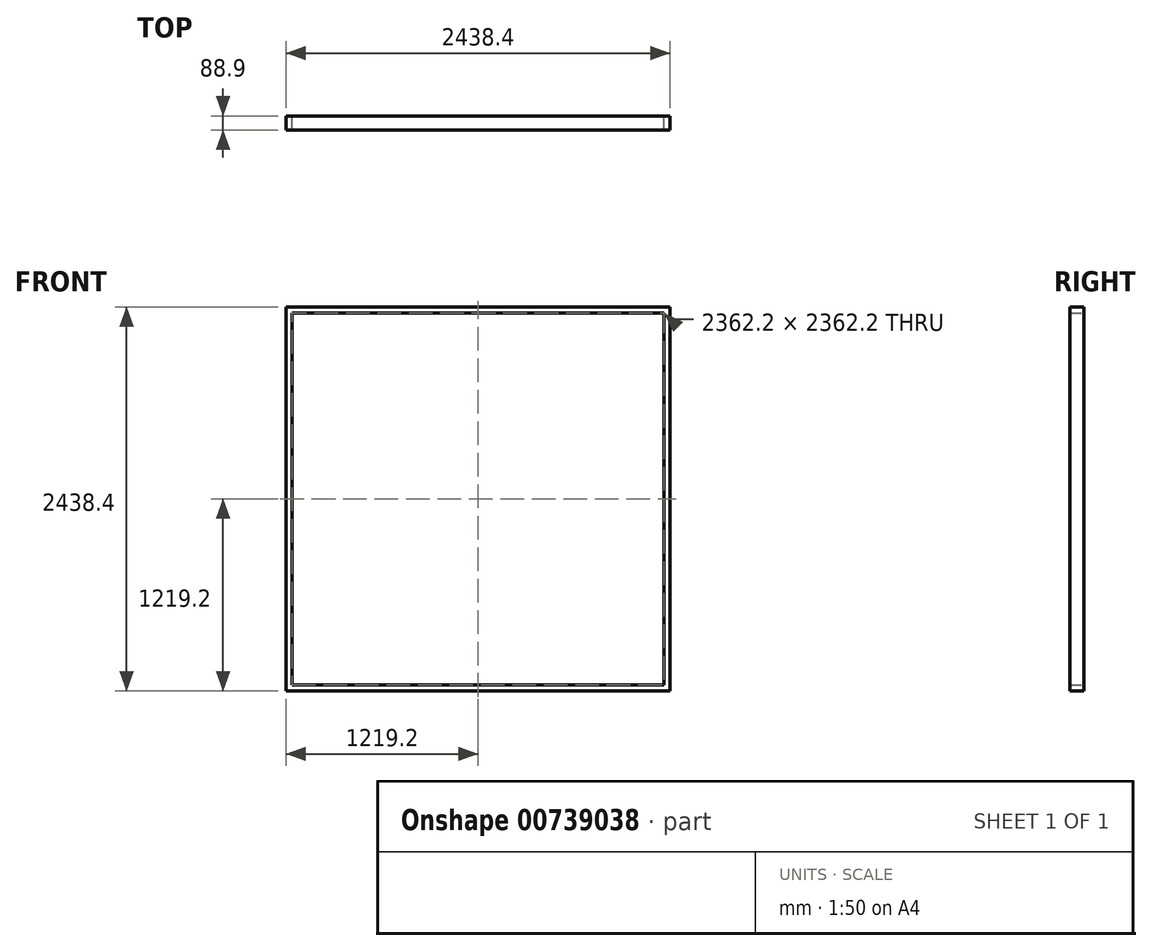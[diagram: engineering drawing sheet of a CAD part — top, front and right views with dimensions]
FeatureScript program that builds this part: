
annotation { "Feature Type Name" : "Feature", "Feature Type Description" : "" }
export const myFeature = defineFeature(function(context is Context, id is Id, definition is map)
    precondition{}
    {
        {
            var Q0;
            Q0=qCreatedBy(makeId("Front.planeOp"),FACE);
            var sketch = newSketch(context, id + "F0", { "sketchPlane" : qUnion([Q0])});
            skLineSegment(sketch, "E0.bottom", {"start": v(-1187.87, 744.67) * mm, "end": v(1250.53, 744.67) * mm});
            skLineSegment(sketch, "E0.top", {"start": v(-1187.87, -1693.73) * mm, "end": v(1250.53, -1693.73) * mm});
            skLineSegment(sketch, "E0.left", {"start": v(-1187.87, 744.67) * mm, "end": v(-1187.87, -1693.73) * mm});
            skLineSegment(sketch, "E0.right", {"start": v(1250.53, 744.67) * mm, "end": v(1250.53, -1693.73) * mm});
            skLineSegment(sketch, "E1.0", {"start": v(-1149.77, 706.57) * mm, "end": v(1164.1, 706.57) * mm});
            skLineSegment(sketch, "E2.0", {"start": v(-1149.77, 706.57) * mm, "end": v(-1149.77, -1655.63) * mm});
            skLineSegment(sketch, "E2.1", {"start": v(-1149.77, 706.57) * mm, "end": v(1212.43, 706.57) * mm});
            skLineSegment(sketch, "E2.2", {"start": v(1212.43, 706.57) * mm, "end": v(1212.43, -1655.63) * mm});
            skLineSegment(sketch, "E2.3", {"start": v(-1149.77, -1655.63) * mm, "end": v(1212.43, -1655.63) * mm});
            skLineSegment(sketch, "E3", {"start": v(-1187.87, 744.67) * mm, "end": v(-1187.87, 1151.07) * mm, "construction": true});
            skLineSegment(sketch, "E4.bottom", {"start": v(-787.82, 706.57) * mm, "end": v(-749.72, 706.57) * mm});
            skLineSegment(sketch, "E4.top", {"start": v(-787.82, -1655.63) * mm, "end": v(-749.72, -1655.63) * mm});
            skLineSegment(sketch, "E4.left", {"start": v(-787.82, 706.57) * mm, "end": v(-787.82, -1655.63) * mm});
            skLineSegment(sketch, "E4.right", {"start": v(-749.72, 706.57) * mm, "end": v(-749.72, -1655.63) * mm});
            skLineSegment(sketch, "E5.bottom", {"start": v(-387.77, 706.57) * mm, "end": v(-349.67, 706.57) * mm});
            skLineSegment(sketch, "E5.top", {"start": v(-387.77, -1655.63) * mm, "end": v(-349.67, -1655.63) * mm});
            skLineSegment(sketch, "E5.left", {"start": v(-387.77, 706.57) * mm, "end": v(-387.77, -1655.63) * mm});
            skLineSegment(sketch, "E5.right", {"start": v(-349.67, 706.57) * mm, "end": v(-349.67, -1655.63) * mm});
            skLineSegment(sketch, "E6.bottom", {"start": v(12.28, 706.57) * mm, "end": v(50.38, 706.57) * mm});
            skLineSegment(sketch, "E6.top", {"start": v(12.28, -1655.63) * mm, "end": v(50.38, -1655.63) * mm});
            skLineSegment(sketch, "E6.left", {"start": v(12.28, 706.57) * mm, "end": v(12.28, -1655.63) * mm});
            skLineSegment(sketch, "E6.right", {"start": v(50.38, 706.57) * mm, "end": v(50.38, -1655.63) * mm});
            skLineSegment(sketch, "E7.bottom", {"start": v(450.43, 706.57) * mm, "end": v(412.33, 706.57) * mm});
            skLineSegment(sketch, "E7.top", {"start": v(450.43, -1655.63) * mm, "end": v(412.33, -1655.63) * mm});
            skLineSegment(sketch, "E7.left", {"start": v(450.43, 706.57) * mm, "end": v(450.43, -1655.63) * mm});
            skLineSegment(sketch, "E7.right", {"start": v(412.33, 706.57) * mm, "end": v(412.33, -1655.63) * mm});
            skLineSegment(sketch, "E8.bottom", {"start": v(812.38, 706.57) * mm, "end": v(850.48, 706.57) * mm});
            skLineSegment(sketch, "E8.top", {"start": v(812.38, -1655.63) * mm, "end": v(850.48, -1655.63) * mm});
            skLineSegment(sketch, "E8.left", {"start": v(812.38, 706.57) * mm, "end": v(812.38, -1655.63) * mm});
            skLineSegment(sketch, "E8.right", {"start": v(850.48, 706.57) * mm, "end": v(850.48, -1655.63) * mm});
            skLineSegment(sketch, "E9.top", {"start": v(-1187.87, 782.77) * mm, "end": v(1250.53, 782.77) * mm});
            skLineSegment(sketch, "E9.left", {"start": v(-1187.87, 744.67) * mm, "end": v(-1187.87, 782.77) * mm});
            skLineSegment(sketch, "E9.right", {"start": v(1250.53, 744.67) * mm, "end": v(1250.53, 782.77) * mm});
            skLineSegment(sketch, "E10", {"start": v(-1187.87, 1151.07) * mm, "end": v(1250.53, 782.77) * mm, "construction": true});
            skLineSegment(sketch, "E11", {"start": v(-1187.87, 1151.07) * mm, "end": v(-1354.44, 1176.23) * mm, "construction": true});
            skLineSegment(sketch, "E12", {"start": v(1250.53, 782.77) * mm, "end": v(1585.43, 732.18) * mm, "construction": true});
            skSolve(sketch);
        }
        {
            var Q0;
            Q0=makeQuery(id+"F0.imprint","IMPRINT",FACE,{"disambiguationData":[TD([[makeQuery(id+"F0.imprint","IMPRINT",EDGE,{"derivedFrom":sQuery(id+"F0.wireOp",EDGE,"E0.bottom")}),1.0]])]});
            var Q1;
            Q1=makeQuery(id+"F0.imprint","IMPRINT",FACE,{"disambiguationData":[TD([[makeQuery(id+"F0.imprint","IMPRINT",EDGE,{"derivedFrom":sQuery(id+"F0.wireOp",EDGE,"E4.bottom")}),-1.0]])]});
            var Q2;
            Q2=makeQuery(id+"F0.imprint","IMPRINT",FACE,{"disambiguationData":[TD([[makeQuery(id+"F0.imprint","IMPRINT",EDGE,{"derivedFrom":sQuery(id+"F0.wireOp",EDGE,"E0.top")}),1.0]])]});
            var Q3;
            Q3=makeQuery(id+"F0.imprint","IMPRINT",FACE,{"disambiguationData":[TD([[makeQuery(id+"F0.imprint","IMPRINT",EDGE,{"derivedFrom":sQuery(id+"F0.wireOp",EDGE,"E5.bottom")}),-1.0]])]});
            var Q4;
            Q4=makeQuery(id+"F0.imprint","IMPRINT",FACE,{"disambiguationData":[TD([[makeQuery(id+"F0.imprint","IMPRINT",EDGE,{"derivedFrom":sQuery(id+"F0.wireOp",EDGE,"E6.bottom")}),-1.0]])]});
            var Q5;
            Q5=makeQuery(id+"F0.imprint","IMPRINT",FACE,{"disambiguationData":[TD([[makeQuery(id+"F0.imprint","IMPRINT",EDGE,{"derivedFrom":sQuery(id+"F0.wireOp",EDGE,"E7.bottom")}),1.0]])]});
            var Q6;
            Q6=makeQuery(id+"F0.imprint","IMPRINT",FACE,{"disambiguationData":[TD([[makeQuery(id+"F0.imprint","IMPRINT",EDGE,{"derivedFrom":sQuery(id+"F0.wireOp",EDGE,"E8.bottom")}),-1.0]])]});
            extrude(context, id + "F1", {"entities" : qUnion([Q0, Q1, Q2, Q3, Q4, Q5, Q6]), "depth" : 88.9 * mm, "offsetDistance" : 25.4 * mm});
        }
    });
